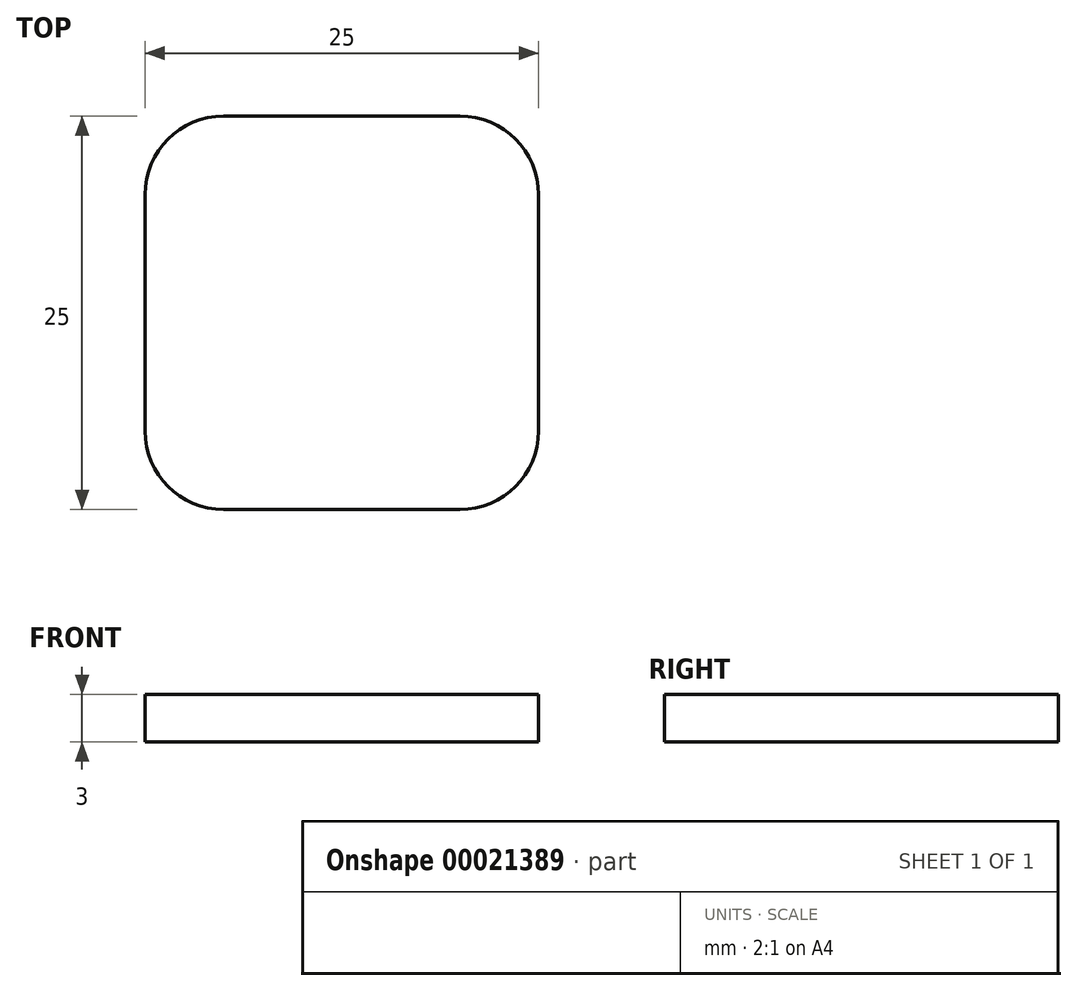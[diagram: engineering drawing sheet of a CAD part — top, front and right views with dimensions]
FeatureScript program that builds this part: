
annotation { "Feature Type Name" : "Feature", "Feature Type Description" : "" }
export const myFeature = defineFeature(function(context is Context, id is Id, definition is map)
    precondition{}
    {
        {
            var Q0;
            Q0=qCreatedBy(makeId("Top.planeOp"),FACE);
            var sketch = newSketch(context, id + "F0", { "sketchPlane" : qUnion([Q0])});
            skLineSegment(sketch, "E0.rect.bottom", {"start": v(-12.5, 12.5) * mm, "end": v(12.5, 12.5) * mm});
            skLineSegment(sketch, "E0.rect.top", {"start": v(-12.5, -12.5) * mm, "end": v(12.5, -12.5) * mm});
            skLineSegment(sketch, "E0.rect.left", {"start": v(-12.5, 12.5) * mm, "end": v(-12.5, -12.5) * mm});
            skLineSegment(sketch, "E0.rect.right", {"start": v(12.5, 12.5) * mm, "end": v(12.5, -12.5) * mm});
            skPoint(sketch, "E0.rect.middle", {"position": v(0, 0) * mm});
            skSolve(sketch);
        }
        {
            var Q0;
            Q0 = qSketchRegion(id + "F0", true);
            extrude(context, id + "F1", {"entities" : qUnion([Q0]), "depth" : 3 * mm});
        }
        {
            var Q0;
            Q0=makeQuery(id+"F1.opExtrude","SWEPT_EDGE",EDGE,{"disambiguationData":[OSD([sQuery(id+"F0.wireOp",EDGE,"E0.rect.top"),sQuery(id+"F0.wireOp",EDGE,"E0.rect.left")])]});
            var Q1;
            Q1=makeQuery(id+"F1.opExtrude","SWEPT_EDGE",EDGE,{"disambiguationData":[OSD([sQuery(id+"F0.wireOp",EDGE,"E0.rect.top"),sQuery(id+"F0.wireOp",EDGE,"E0.rect.right")])]});
            var Q2;
            Q2=makeQuery(id+"F1.opExtrude","SWEPT_EDGE",EDGE,{"disambiguationData":[OSD([sQuery(id+"F0.wireOp",EDGE,"E0.rect.bottom"),sQuery(id+"F0.wireOp",EDGE,"E0.rect.right")])]});
            var Q3;
            Q3=makeQuery(id+"F1.opExtrude","SWEPT_EDGE",EDGE,{"disambiguationData":[OSD([sQuery(id+"F0.wireOp",EDGE,"E0.rect.bottom"),sQuery(id+"F0.wireOp",EDGE,"E0.rect.left")])]});
            fillet(context, id + "F2", {"entities" : qUnion([Q0, Q1, Q2, Q3]), "radius" : 5 * mm, "tangentPropagation" : true, "allowEdgeOverflow" : false});
        }
    });
